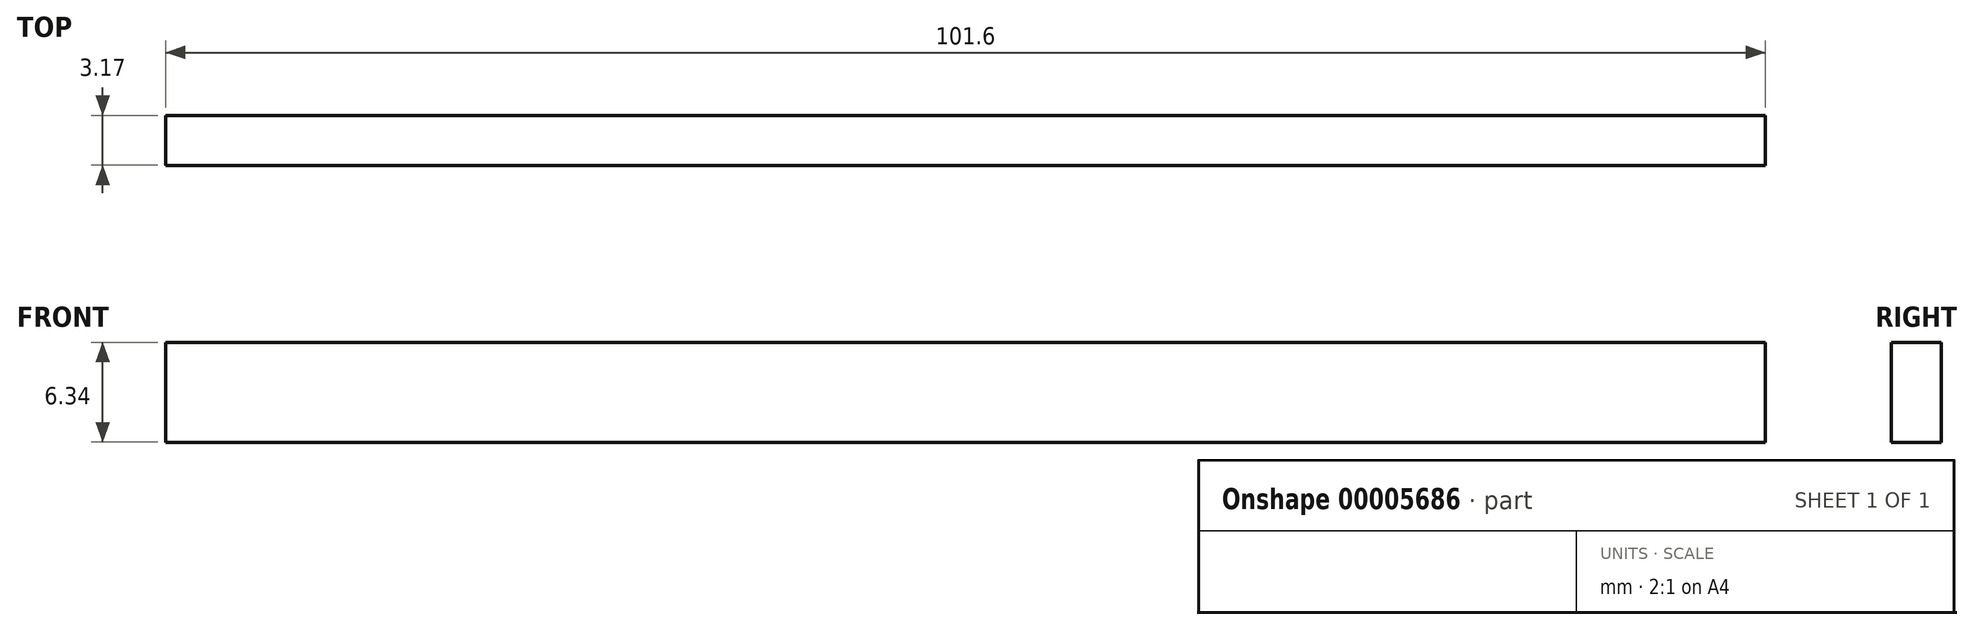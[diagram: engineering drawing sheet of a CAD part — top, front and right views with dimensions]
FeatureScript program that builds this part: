
annotation { "Feature Type Name" : "Feature", "Feature Type Description" : "" }
export const myFeature = defineFeature(function(context is Context, id is Id, definition is map)
    precondition{}
    {
        {
            var Q0;
            Q0=qCreatedBy(makeId("Front.planeOp"),FACE);
            var sketch = newSketch(context, id + "F0", { "sketchPlane" : qUnion([Q0])});
            skLineSegment(sketch, "E0.rect.bottom", {"start": v(50.8, 3.18) * mm, "end": v(-50.8, 3.18) * mm});
            skLineSegment(sketch, "E0.rect.top", {"start": v(50.8, -3.17) * mm, "end": v(-50.8, -3.17) * mm});
            skLineSegment(sketch, "E0.rect.left", {"start": v(50.8, 3.18) * mm, "end": v(50.8, -3.18) * mm});
            skLineSegment(sketch, "E0.rect.right", {"start": v(-50.8, 3.18) * mm, "end": v(-50.8, -3.18) * mm});
            skPoint(sketch, "E0.rect.middle", {"position": v(0, 0) * mm});
            skSolve(sketch);
        }
        {
            var Q0;
            Q0 = qSketchRegion(id + "F0", true);
            extrude(context, id + "F1", {"entities" : qUnion([Q0]), "depth" : 3.17 * mm});
        }
    });
